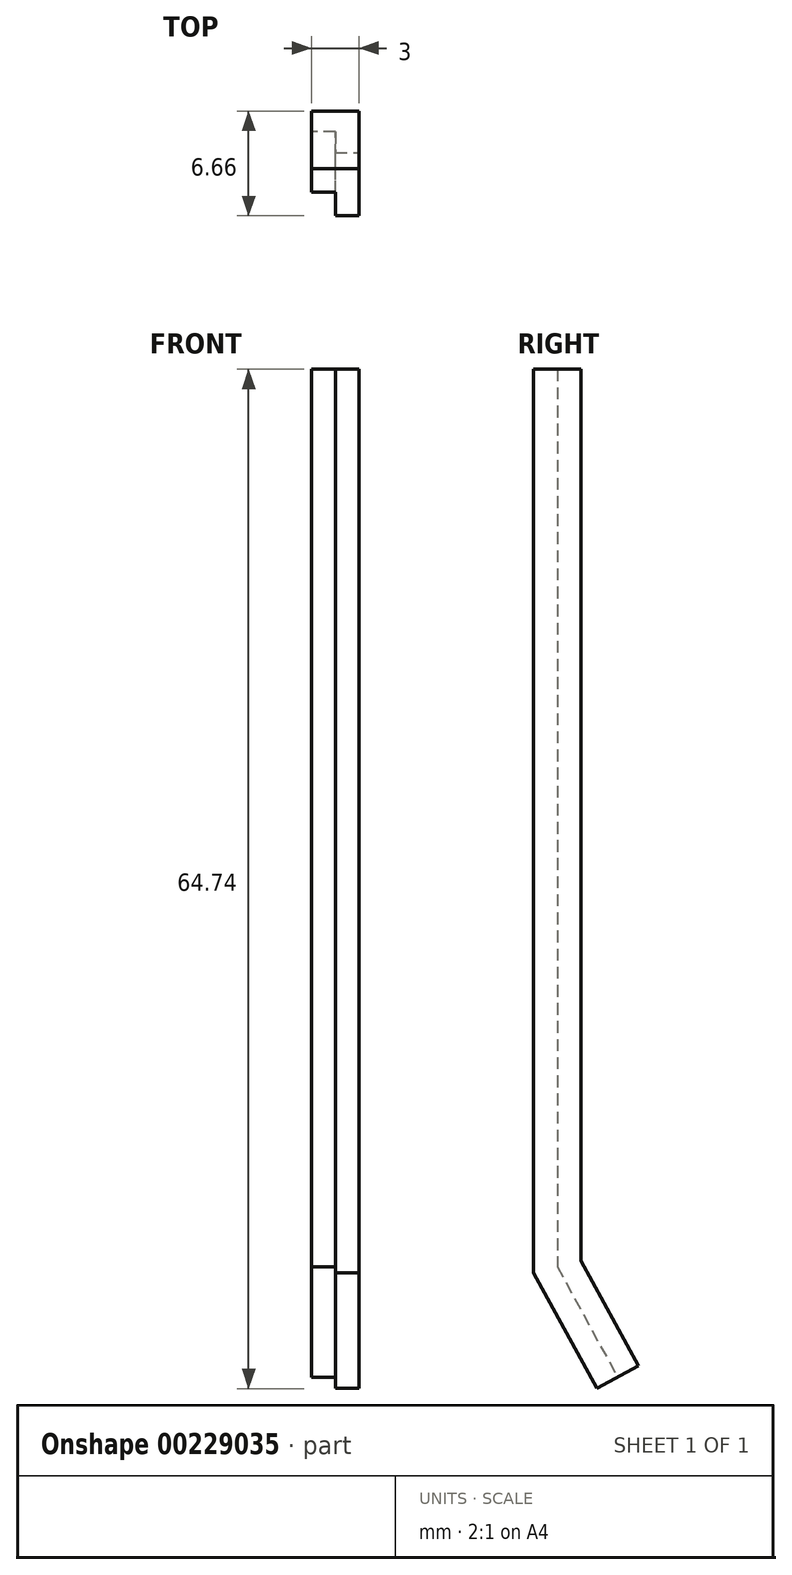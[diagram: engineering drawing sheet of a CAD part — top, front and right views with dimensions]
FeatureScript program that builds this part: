
annotation { "Feature Type Name" : "Feature", "Feature Type Description" : "" }
export const myFeature = defineFeature(function(context is Context, id is Id, definition is map)
    precondition{}
    {
        {
            var Q0;
            Q0=qCreatedBy(makeId("Top.planeOp"),FACE);
            var sketch = newSketch(context, id + "F0", { "sketchPlane" : qUnion([Q0])});
            skLineSegment(sketch, "E0.0.left", {"start": v(1.5, 1.5) * mm, "end": v(2.17, 1.5) * mm});
            skLineSegment(sketch, "E0.0.right", {"start": v(1.5, -1.5) * mm, "end": v(2.17, -1.5) * mm});
            skLineSegment(sketch, "E0.1.left", {"start": v(1.5, -1.5) * mm, "end": v(1.5, -2.17) * mm});
            skLineSegment(sketch, "E0.1.right", {"start": v(-1.5, -1.5) * mm, "end": v(-1.5, -2.17) * mm});
            skLineSegment(sketch, "E0.2.left", {"start": v(-1.5, -1.5) * mm, "end": v(-2.17, -1.5) * mm});
            skLineSegment(sketch, "E0.2.right", {"start": v(-1.5, 1.5) * mm, "end": v(-2.17, 1.5) * mm});
            skLineSegment(sketch, "E1", {"start": v(0, 0) * mm, "end": v(0, 2.17) * mm});
            skLineSegment(sketch, "E2", {"start": v(0, 0) * mm, "end": v(2.17, 0) * mm});
            skLineSegment(sketch, "E3", {"start": v(0, 0) * mm, "end": v(0, -2.17) * mm});
            skLineSegment(sketch, "E4", {"start": v(0, 0) * mm, "end": v(-2.17, 0) * mm});
            skArc(sketch, "E5.0.startCap", {"start": v(1.5, 0) * mm, "mid": v(0, -1.5) * mm, "end": v(-1.5, 0) * mm});
            skArc(sketch, "E5.0.endCap", {"start": v(-1.5, 2.17) * mm, "mid": v(0, 3.67) * mm, "end": v(1.5, 2.17) * mm});
            skLineSegment(sketch, "E5.0.left", {"start": v(-1.5, 0) * mm, "end": v(-1.5, 2.17) * mm});
            skLineSegment(sketch, "E5.0.right", {"start": v(1.5, 0) * mm, "end": v(1.5, 2.17) * mm});
            skArc(sketch, "E5.1.startCap", {"start": v(0, -1.5) * mm, "mid": v(-1.5, 0) * mm, "end": v(0, 1.5) * mm});
            skArc(sketch, "E5.1.endCap", {"start": v(2.17, 1.5) * mm, "mid": v(3.67, 0) * mm, "end": v(2.17, -1.5) * mm});
            skLineSegment(sketch, "E5.1.left", {"start": v(0, 1.5) * mm, "end": v(2.17, 1.5) * mm});
            skLineSegment(sketch, "E5.1.right", {"start": v(0, -1.5) * mm, "end": v(2.17, -1.5) * mm});
            skArc(sketch, "E5.2.startCap", {"start": v(-1.5, 0) * mm, "mid": v(0, 1.5) * mm, "end": v(1.5, 0) * mm});
            skArc(sketch, "E5.2.endCap", {"start": v(1.5, -2.17) * mm, "mid": v(0, -3.67) * mm, "end": v(-1.5, -2.17) * mm});
            skLineSegment(sketch, "E5.2.left", {"start": v(1.5, 0) * mm, "end": v(1.5, -2.17) * mm});
            skLineSegment(sketch, "E5.2.right", {"start": v(-1.5, 0) * mm, "end": v(-1.5, -2.17) * mm});
            skArc(sketch, "E5.3.startCap", {"start": v(0, 1.5) * mm, "mid": v(1.5, 0) * mm, "end": v(0, -1.5) * mm});
            skArc(sketch, "E5.3.endCap", {"start": v(-2.17, -1.5) * mm, "mid": v(-3.67, 0) * mm, "end": v(-2.17, 1.5) * mm});
            skLineSegment(sketch, "E5.3.left", {"start": v(0, -1.5) * mm, "end": v(-2.17, -1.5) * mm});
            skLineSegment(sketch, "E5.3.right", {"start": v(0, 1.5) * mm, "end": v(-2.17, 1.5) * mm});
            skSolve(sketch);
        }
        {
            var Q0;
            Q0=qCreatedBy(makeId("Right.planeOp"),FACE);
            var sketch = newSketch(context, id + "F1", { "sketchPlane" : qUnion([Q0])});
            skLineSegment(sketch, "E6", {"start": v(0, 0) * mm, "end": v(0, -57) * mm});
            skLineSegment(sketch, "E7", {"start": v(0, -57) * mm, "end": v(3.84, -64.02) * mm});
            skSolve(sketch);
        }
        {
            var Q0;
            {var subQ3=sQuery(id+"F0.wireOp",EDGE,"E5.1.startCap");Q0=makeQuery(id+"F0.imprint","IMPRINT",FACE,{"disambiguationData":[TD([[makeQuery(id+"F0.imprint","IMPRINT",EDGE,{"derivedFrom":subQ3}),-1.0]])]});}
            var Q1;
            {var subQ1=sQuery(id+"F0.wireOp",EDGE,"E5.3.endCap");Q1=makeQuery(id+"F0.imprint","IMPRINT",FACE,{"disambiguationData":[TD([[makeQuery(id+"F0.imprint","IMPRINT",EDGE,{"derivedFrom":subQ1}),-1.0]])]});}
            var Q2;
            {var subQ3=sQuery(id+"F0.wireOp",EDGE,"E5.2.startCap");Q2=makeQuery(id+"F0.imprint","IMPRINT",FACE,{"disambiguationData":[TD([[makeQuery(id+"F0.imprint","IMPRINT",EDGE,{"derivedFrom":subQ3}),-1.0]])]});}
            var Q3;
            {var subQ1=sQuery(id+"F0.wireOp",EDGE,"E5.1.right");var subQ3=sQuery(id+"F0.wireOp",EDGE,"E5.2.left");var subQ4=makeQuery(id+"F0.imprint","INTERSECT",VERTEX,{"derivedFrom":[subQ1,subQ3]});Q3=makeQuery(id+"F0.imprint","IMPRINT",FACE,{"disambiguationData":[TD([[makeQuery(id+"F0.imprint","IMPRINT",EDGE,{"disambiguationData":[TD([[subQ4,1.0]])],"derivedFrom":subQ3}),-1.0]])]});}
            var Q4;
            {var subQ0=sQuery(id+"F0.wireOp",EDGE,"E5.1.startCap");Q4=makeQuery(id+"F0.imprint","IMPRINT",FACE,{"disambiguationData":[TD([[makeQuery(id+"F0.imprint","IMPRINT",EDGE,{"derivedFrom":subQ0}),1.0]])]});}
            var Q5;
            {var subQ1=sQuery(id+"F0.wireOp",EDGE,"E5.2.endCap");Q5=makeQuery(id+"F0.imprint","IMPRINT",FACE,{"disambiguationData":[TD([[makeQuery(id+"F0.imprint","IMPRINT",EDGE,{"derivedFrom":subQ1}),-1.0]])]});}
            var Q6;
            {var subQ1=sQuery(id+"F0.wireOp",EDGE,"E5.1.endCap");Q6=makeQuery(id+"F0.imprint","IMPRINT",FACE,{"disambiguationData":[TD([[makeQuery(id+"F0.imprint","IMPRINT",EDGE,{"derivedFrom":subQ1}),-1.0]])]});}
            var Q7;
            {var subQ0=sQuery(id+"F0.wireOp",EDGE,"E3");var subQ1=sQuery(id+"F0.wireOp",EDGE,"E2");var subQ2=makeQuery(id+"F0.imprint","INTERSECT",VERTEX,{"derivedFrom":[sQuery(id+"F0.wireOp",EDGE,"E1"),subQ1,subQ0,sQuery(id+"F0.wireOp",EDGE,"E4")]});Q7=makeQuery(id+"F0.imprint","IMPRINT",FACE,{"disambiguationData":[TD([[makeQuery(id+"F0.imprint","IMPRINT",EDGE,{"disambiguationData":[TD([[subQ2,-1.0]])],"derivedFrom":subQ1}),-1.0]])]});}
            var Q8;
            {var subQ1=sQuery(id+"F0.wireOp",EDGE,"E5.0.right");var subQ3=sQuery(id+"F0.wireOp",EDGE,"E5.1.left");var subQ4=makeQuery(id+"F0.imprint","INTERSECT",VERTEX,{"derivedFrom":[subQ1,subQ3]});Q8=makeQuery(id+"F0.imprint","IMPRINT",FACE,{"disambiguationData":[TD([[makeQuery(id+"F0.imprint","IMPRINT",EDGE,{"disambiguationData":[TD([[subQ4,1.0]])],"derivedFrom":subQ1}),1.0]])]});}
            var Q9;
            {var subQ0=sQuery(id+"F0.wireOp",EDGE,"E5.2.startCap");Q9=makeQuery(id+"F0.imprint","IMPRINT",FACE,{"disambiguationData":[TD([[makeQuery(id+"F0.imprint","IMPRINT",EDGE,{"derivedFrom":subQ0}),1.0]])]});}
            var Q10;
            {var subQ0=sQuery(id+"F0.wireOp",EDGE,"E2");var subQ1=sQuery(id+"F0.wireOp",EDGE,"E1");var subQ2=makeQuery(id+"F0.imprint","INTERSECT",VERTEX,{"derivedFrom":[subQ1,subQ0,sQuery(id+"F0.wireOp",EDGE,"E3"),sQuery(id+"F0.wireOp",EDGE,"E4")]});Q10=makeQuery(id+"F0.imprint","IMPRINT",FACE,{"disambiguationData":[TD([[makeQuery(id+"F0.imprint","IMPRINT",EDGE,{"disambiguationData":[TD([[subQ2,-1.0]])],"derivedFrom":subQ0}),1.0]])]});}
            var Q11;
            {var subQ5=sQuery(id+"F0.wireOp",EDGE,"E5.0.endCap");Q11=makeQuery(id+"F0.imprint","IMPRINT",FACE,{"disambiguationData":[TD([[makeQuery(id+"F0.imprint","IMPRINT",EDGE,{"derivedFrom":subQ5}),-1.0]])]});}
            var Q12;
            Q12=sQuery(id+"F1.wireOp",EDGE,"E6");
            var Q13;
            Q13=sQuery(id+"F1.wireOp",EDGE,"E7");
            sweep(context, id + "F2", {"profiles" : qUnion([Q0, Q1, Q2, Q3, Q4, Q5, Q6, Q7, Q8, Q9, Q10, Q11]), "path" : qUnion([Q12, Q13])});
        }
    });
